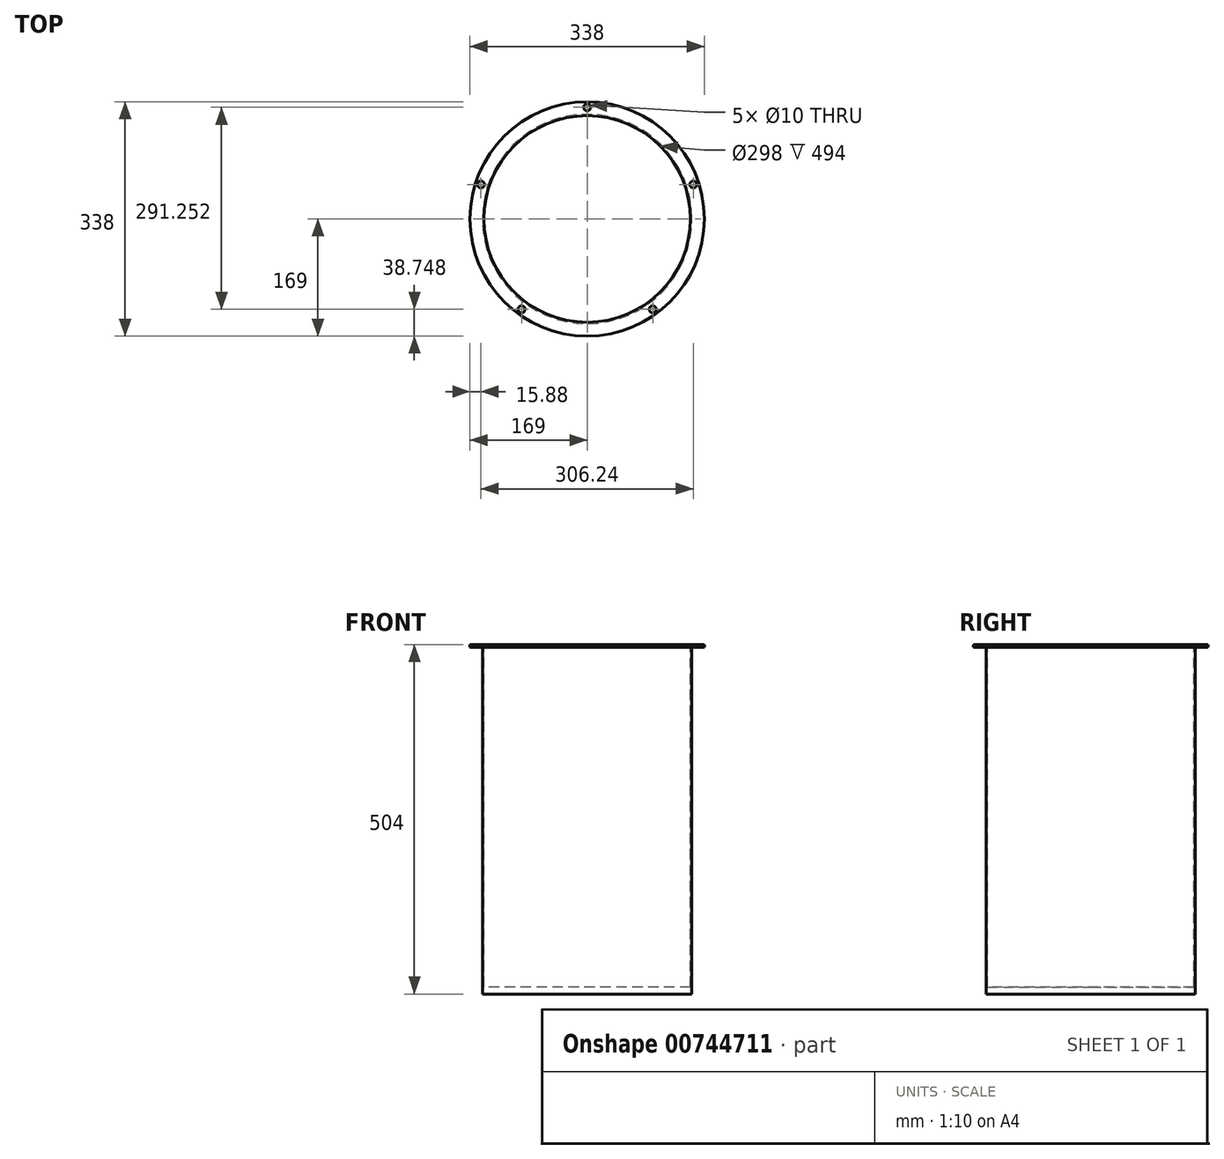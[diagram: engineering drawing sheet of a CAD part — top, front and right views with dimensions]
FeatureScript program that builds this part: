
annotation { "Feature Type Name" : "Feature", "Feature Type Description" : "" }
export const myFeature = defineFeature(function(context is Context, id is Id, definition is map)
    precondition{}
    {
        {
            var Q0;
            Q0=qCreatedBy(makeId("Top.planeOp"),FACE);
            var sketch = newSketch(context, id + "F0", { "sketchPlane" : qUnion([Q0])});
            skCircle(sketch, "E0", {"center": v(0, 0) * mm, "radius": 151 * mm});
            skSolve(sketch);
        }
        {
            var Q0;
            Q0=makeQuery(id+"F0.imprint","IMPRINT",FACE,{"disambiguationData":[TD([[makeQuery(id+"F0.imprint","IMPRINT",EDGE,{"derivedFrom":sQuery(id+"F0.wireOp",EDGE,"E0")}),1.0]])]});
            extrude(context, id + "F1", {"entities" : qUnion([Q0]), "depth" : 500 * mm, "offsetDistance" : 25 * mm});
        }
        {
            var Q0;
            Q0=makeQuery(id+"F1.opExtrude","CAP_FACE",FACE,{"disambiguationData":[OSD([sQuery(id+"F0.wireOp",EDGE,"E0")])],"isStart":false});
            var sketch = newSketch(context, id + "F2", { "sketchPlane" : qUnion([Q0])});
            skCircle(sketch, "E1", {"center": v(0, 0) * mm, "radius": 149 * mm});
            skSolve(sketch);
        }
        {
            var Q0;
            Q0=makeQuery(id+"F2.imprint","IMPRINT",FACE,{"disambiguationData":[TD([[makeQuery(id+"F2.imprint","IMPRINT",EDGE,{"derivedFrom":sQuery(id+"F2.wireOp",EDGE,"E1")}),1.0]])]});
            extrude(context, id + "F3", {"entities" : qUnion([Q0]), "operationType" : NewBodyOperationType.REMOVE, "oppositeDirection" : true, "depth" : 490 * mm, "offsetDistance" : 25 * mm});
        }
        {
            var Q0;
            Q0=makeQuery(id+"F1.opExtrude","CAP_FACE",FACE,{"disambiguationData":[OSD([sQuery(id+"F0.wireOp",EDGE,"E0")])],"isStart":false});
            var sketch = newSketch(context, id + "F4", { "sketchPlane" : qUnion([Q0])});
            skCircle(sketch, "E2", {"center": v(0, 0) * mm, "radius": 169 * mm});
            skCircle(sketch, "E3", {"center": v(0, 0) * mm, "radius": 149 * mm});
            skSolve(sketch);
        }
        {
            var Q0;
            Q0 = qSketchRegion(id + "F4", true);
            extrude(context, id + "F5", {"entities" : qUnion([Q0]), "operationType" : NewBodyOperationType.ADD, "depth" : 4 * mm, "offsetDistance" : 25 * mm});
        }
        {
            var Q0;
            Q0=makeQuery(id+"F5.opExtrude","CAP_FACE",FACE,{"disambiguationData":[OSD([sQuery(id+"F4.wireOp",EDGE,"E2"),sQuery(id+"F4.wireOp",EDGE,"E3")])],"isStart":false});
            var sketch = newSketch(context, id + "F6", { "sketchPlane" : qUnion([Q0])});
            skCircle(sketch, "E4", {"center": v(0, 161) * mm, "radius": 5 * mm});
            skCircle(sketch, "E5.1.0", {"center": v(-153.12, 49.75) * mm, "radius": 5 * mm});
            skCircle(sketch, "E5.2.0", {"center": v(-94.63, -130.25) * mm, "radius": 5 * mm});
            skCircle(sketch, "E5.3.0", {"center": v(94.63, -130.25) * mm, "radius": 5 * mm});
            skCircle(sketch, "E5.4.0", {"center": v(153.12, 49.75) * mm, "radius": 5 * mm});
            skPoint(sketch, "E5.center", {"position": v(0, 0) * mm});
            skSolve(sketch);
        }
        {
            var Q0;
            Q0 = qSketchRegion(id + "F6", true);
            extrude(context, id + "F7", {"entities" : qUnion([Q0]), "operationType" : NewBodyOperationType.REMOVE, "endBound" : BoundingType.THROUGH_ALL, "oppositeDirection" : true, "depth" : 25 * mm, "offsetDistance" : 25 * mm});
        }
    });
